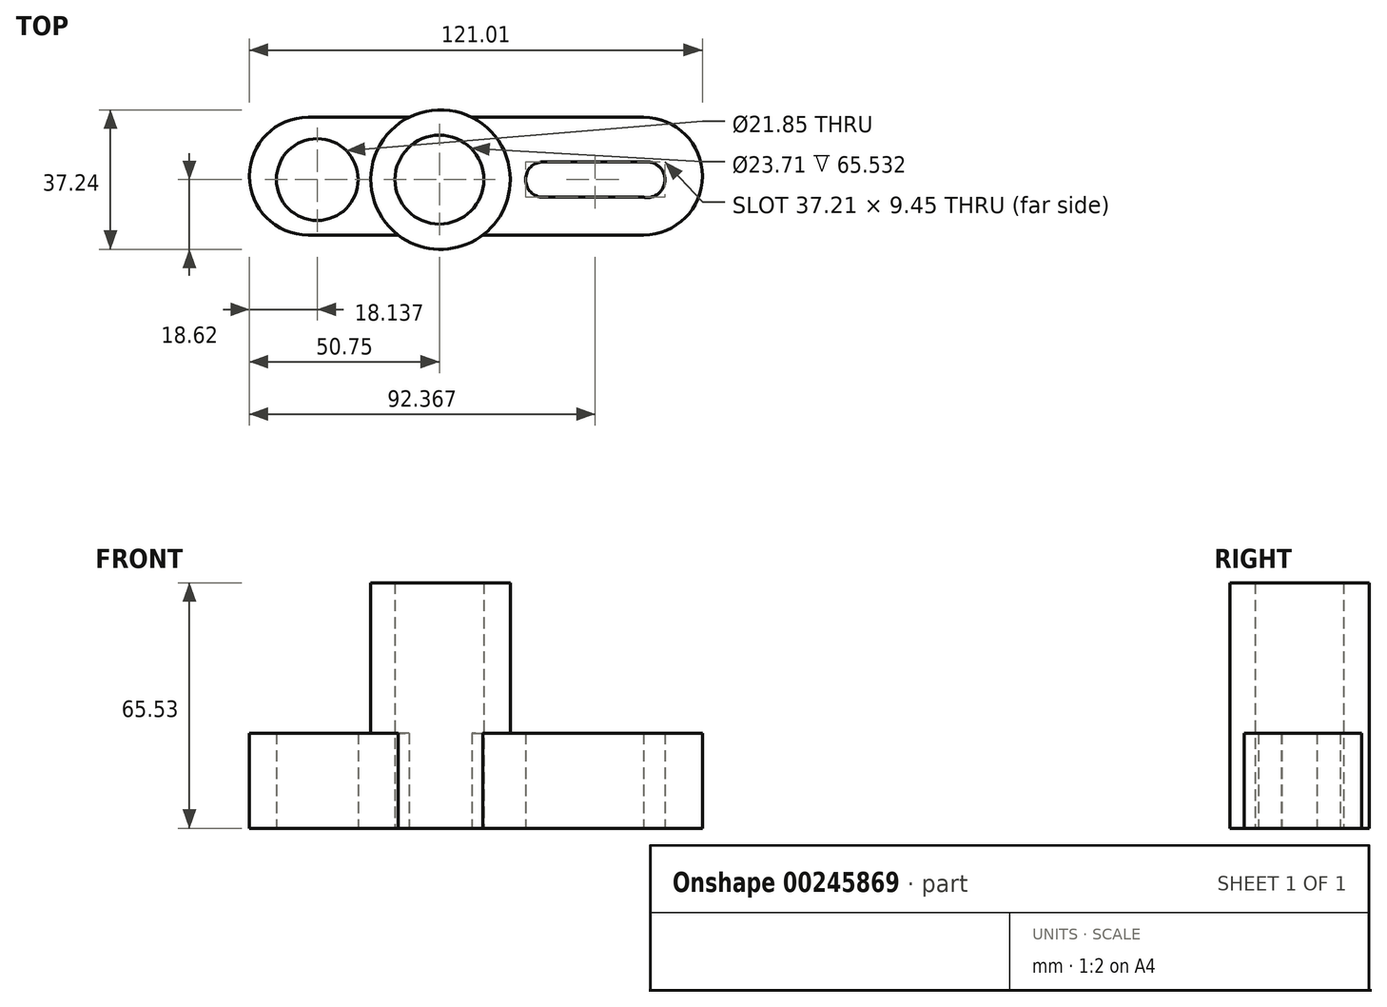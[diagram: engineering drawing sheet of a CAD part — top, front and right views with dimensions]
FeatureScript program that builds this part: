
annotation { "Feature Type Name" : "Feature", "Feature Type Description" : "" }
export const myFeature = defineFeature(function(context is Context, id is Id, definition is map)
    precondition{}
    {
        {
            var Q0;
            Q0=qCreatedBy(makeId("Top.planeOp"),FACE);
            var sketch = newSketch(context, id + "F0", { "sketchPlane" : qUnion([Q0])});
            skLineSegment(sketch, "E0", {"start": v(38.7, -14.78) * mm, "end": v(-50.9, -14.78) * mm});
            skLineSegment(sketch, "E1", {"start": v(-50.9, 16.61) * mm, "end": v(38.7, 16.61) * mm});
            skArc(sketch, "E2", {"start": v(-50.9, 16.61) * mm, "mid": v(-66.6, 0.91) * mm, "end": v(-50.9, -14.78) * mm});
            skArc(sketch, "E3", {"start": v(38.7, -14.78) * mm, "mid": v(54.4, 0.91) * mm, "end": v(38.7, 16.61) * mm});
            skLineSegment(sketch, "E4", {"start": v(11.89, 4.72) * mm, "end": v(39.62, 4.72) * mm});
            skLineSegment(sketch, "E5", {"start": v(38.7, -4.72) * mm, "end": v(11.89, -4.72) * mm});
            skArc(sketch, "E6", {"start": v(11.89, 4.72) * mm, "mid": v(7.16, 0) * mm, "end": v(11.89, -4.72) * mm});
            skArc(sketch, "E7", {"start": v(38.7, -4.72) * mm, "mid": v(44.37, -0.5) * mm, "end": v(39.62, 4.72) * mm});
            skCircle(sketch, "E8", {"center": v(-48.46, 0) * mm, "radius": 10.93 * mm});
            skSolve(sketch);
        }
        {
            var Q0;
            Q0=qCreatedBy(makeId("Top.planeOp"),FACE);
            var sketch = newSketch(context, id + "F1", { "sketchPlane" : qUnion([Q0])});
            skCircle(sketch, "E9", {"center": v(-15.54, 0) * mm, "radius": 18.62 * mm});
            skSolve(sketch);
        }
        {
            var Q0;
            Q0 = qSketchRegion(id + "F0", true);
            extrude(context, id + "F2", {"entities" : qUnion([Q0]), "depth" : 25.4 * mm});
        }
        {
            var Q0;
            Q0 = qSketchRegion(id + "F1", true);
            extrude(context, id + "F3", {"entities" : qUnion([Q0]), "operationType" : NewBodyOperationType.ADD, "depth" : 65.53 * mm});
        }
        {
            var Q0;
            Q0=qCreatedBy(makeId("Top.planeOp"),FACE);
            var sketch = newSketch(context, id + "F4", { "sketchPlane" : qUnion([Q0])});
            skCircle(sketch, "E10", {"center": v(-15.85, 0) * mm, "radius": 11.86 * mm});
            skSolve(sketch);
        }
        {
            var Q0;
            Q0 = qSketchRegion(id + "F4", true);
            extrude(context, id + "F5", {"entities" : qUnion([Q0]), "operationType" : NewBodyOperationType.REMOVE, "depth" : 104.9 * mm});
        }
    });
